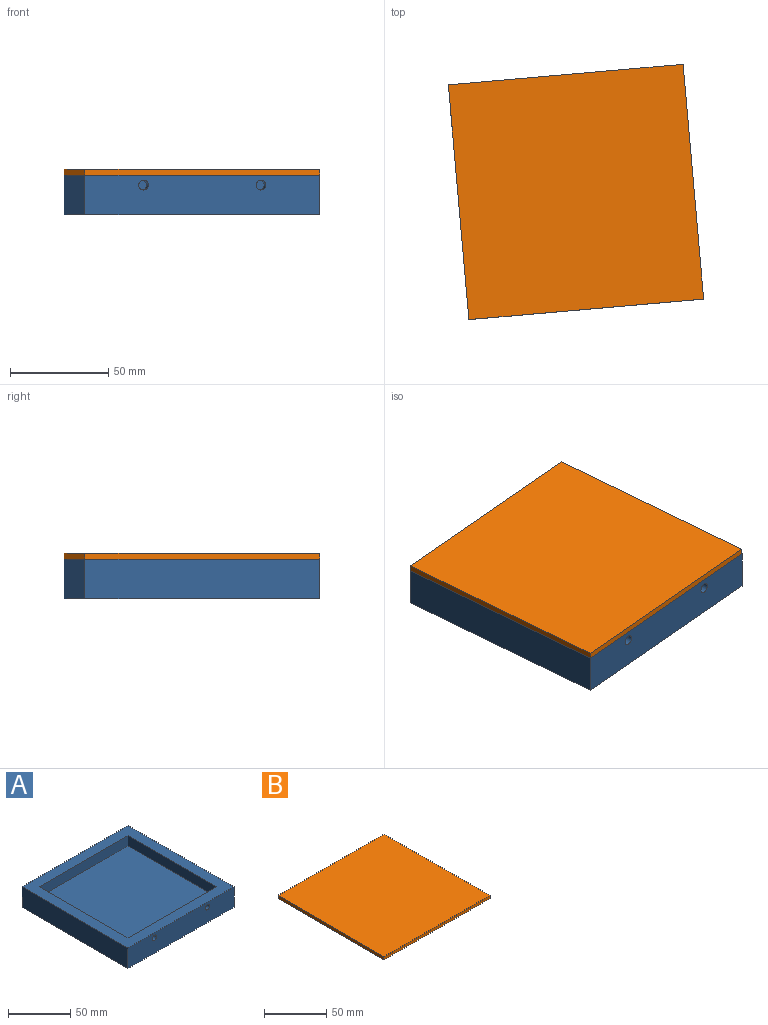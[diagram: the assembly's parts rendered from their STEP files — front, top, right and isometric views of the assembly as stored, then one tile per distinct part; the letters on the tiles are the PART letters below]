
ASSEMBLY  parts=2 mates=1
PART A: 13 faces, bbox 120x120x20 mm
  f0: plane 120x20mm, normal (1,0,0), area 2400mm2, adj f1,f3,f4,f9
  f1: plane 120x20mm, normal (0,1,0), area 2400mm2, adj f0,f2,f4,f9
  f2: plane 120x20mm, normal (-1,0,0), area 2400mm2, adj f1,f3,f4,f9
  f3: plane 120x20mm, normal (0,-1,0), area 2360.7mm2, adj f0,f2,f4,f9,f11,f12
  f4: plane 120x120mm, normal (0,0,-1), area 14400mm2, adj f0,f1,f2,f3
  f5: plane 100x10mm, normal (0,-1,0), area 1000mm2, adj f6,f8,f9,f10
  f6: plane 100x10mm, normal (-1,0,0), area 1000mm2, adj f5,f7,f9,f10
  f7: plane 100x10mm, normal (0,1,0), area 960.7mm2, adj f6,f8,f9,f10,f11,f12
  f8: plane 100x10mm, normal (1,0,0), area 1000mm2, adj f5,f7,f9,f10
  f9: plane 120x120mm, normal (0,0,1), area 4400mm2, adj f0,f1,f2,f3,f5,f6,f7,f8
  f10: plane 100x100mm, normal (0,0,1), area 10000mm2, adj f5,f6,f7,f8
  f11: cylinder r=2.5mm len=10mm, axis (0,-1,0), area 157.1mm2, adj f3,f7
  f12: cylinder r=2.5mm len=10mm, axis (0,-1,0), area 157.1mm2, adj f3,f7
PART B: 6 faces, bbox 120x120x3 mm
  f0: plane 120x3mm, normal (0,1,0), area 360mm2, adj f1,f3,f4,f5
  f1: plane 120x3mm, normal (-1,0,0), area 360mm2, adj f0,f2,f4,f5
  f2: plane 120x3mm, normal (0,-1,0), area 360mm2, adj f1,f3,f4,f5
  f3: plane 120x3mm, normal (1,0,0), area 360mm2, adj f0,f2,f4,f5
  f4: plane 120x120mm, normal (0,0,1), area 14400mm2, adj f0,f1,f2,f3
  f5: plane 120x120mm, normal (0,0,-1), area 14400mm2, adj f0,f1,f2,f3
PLACE A rot(axis=(0,0,1),5deg) t=(19.14,13.76,26.99)mm
PLACE B rot(axis=(0,0,1),5deg) t=(-125.24,-11.12,36.99)mm
MATE planar A.f9 <-> B.f5  axis (0,0,1) through (-35.4,-51.24,36.99)mm
